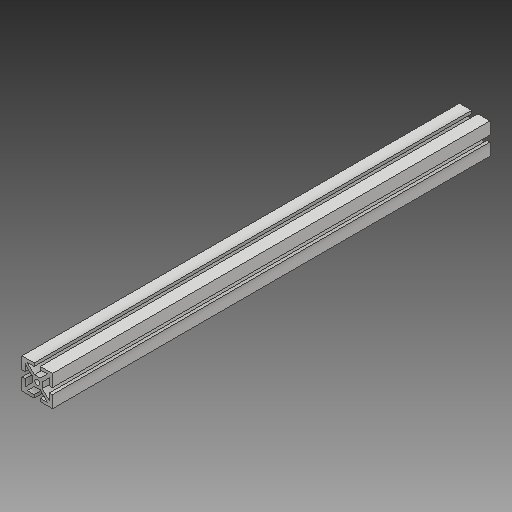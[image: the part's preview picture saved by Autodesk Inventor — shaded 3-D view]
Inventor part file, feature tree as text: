
AUTODESK INVENTOR PART (.ipt)
format: ipt  version: 2018 (Build 220112000, 112)  size: 149,504 bytes
history: native  units: mm
features: extrude x1, sketch x1
ambient origin geometry x8: Origin, YZ Plane, XZ Plane, XY Plane, X Axis, Y Axis, Z Axis, Center Point
bodies: Volumenkörper1 (feature_tree)
feature tree (2):
  extrude  "Extrusion1"  Depth=3.0mm
  sketch  "Skizze1"  dims[d0=3.0mm d1=3.0mm d2=0.5mm d3=1.0mm d4=1.0mm d5=1.2mm d6=1.2mm d7=1.2mm d8=1.2mm d9=0.3mm d10=0.15mm d11=0.15mm d12=0.15mm d13=0.15mm d14=43.0mm d15=0.0mm]
